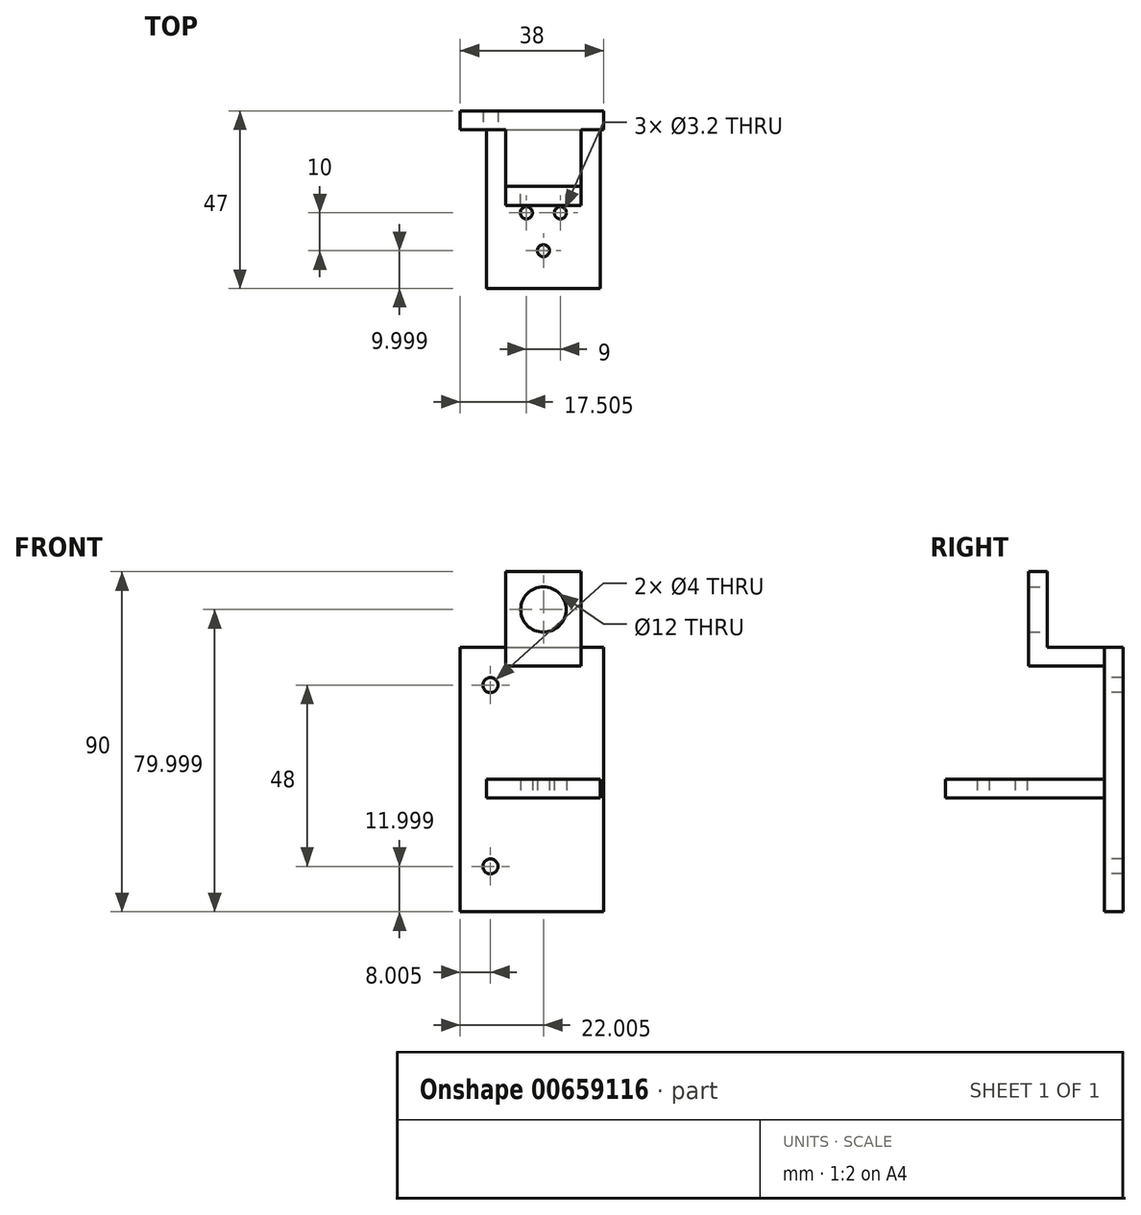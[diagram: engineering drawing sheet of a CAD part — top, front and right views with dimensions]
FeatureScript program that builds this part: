
annotation { "Feature Type Name" : "Feature", "Feature Type Description" : "" }
export const myFeature = defineFeature(function(context is Context, id is Id, definition is map)
    precondition{}
    {
        {
            var Q0;
            Q0=qCreatedBy(makeId("Top.planeOp"),FACE);
            var sketch = newSketch(context, id + "F0", { "sketchPlane" : qUnion([Q0])});
            skLineSegment(sketch, "E0.bottom", {"start": v(-60.29, 32.76) * mm, "end": v(-30.29, 32.76) * mm});
            skLineSegment(sketch, "E0.top", {"start": v(-60.29, 2.76) * mm, "end": v(-30.29, 2.76) * mm});
            skLineSegment(sketch, "E0.left", {"start": v(-60.29, 32.76) * mm, "end": v(-60.29, 2.76) * mm});
            skLineSegment(sketch, "E0.right", {"start": v(-30.29, 32.76) * mm, "end": v(-30.29, 2.76) * mm});
            skCircle(sketch, "E1", {"center": v(-49.79, 22.76) * mm, "radius": 1.6 * mm});
            skCircle(sketch, "E2", {"center": v(-40.79, 22.76) * mm, "radius": 1.6 * mm});
            skCircle(sketch, "E3", {"center": v(-45.29, 12.76) * mm, "radius": 1.6 * mm});
            skSolve(sketch);
        }
        {
            var Q0;
            Q0=makeQuery(id+"F0.imprint","IMPRINT",FACE,{"disambiguationData":[TD([[makeQuery(id+"F0.imprint","IMPRINT",EDGE,{"derivedFrom":sQuery(id+"F0.wireOp",EDGE,"E0.bottom")}),-1.0]])]});
            extrude(context, id + "F1", {"entities" : qUnion([Q0]), "depth" : 5 * mm, "offsetDistance" : 25 * mm});
        }
        {
            var Q0;
            Q0=makeQuery(id+"F1.opExtrude","SWEPT_FACE",FACE,{"disambiguationData":[OSD([sQuery(id+"F0.wireOp",EDGE,"E0.bottom")])]});
            extrude(context, id + "F2", {"entities" : qUnion([Q0]), "operationType" : NewBodyOperationType.ADD, "depth" : 12 * mm, "offsetDistance" : 25 * mm});
        }
        {
            var Q0;
            Q0=makeQuery(id+"F2.opExtrude","CAP_FACE",FACE,{"disambiguationData":[OSD([sQuery(id+"F0.wireOp",EDGE,"E0.bottom")])],"isStart":false});
            var sketch = newSketch(context, id + "F3", { "sketchPlane" : qUnion([Q0])});
            skLineSegment(sketch, "E4.bottom", {"start": v(67.29, -30.11) * mm, "end": v(29.29, -30.11) * mm});
            skLineSegment(sketch, "E4.top", {"start": v(67.29, 34.89) * mm, "end": v(29.29, 34.89) * mm});
            skLineSegment(sketch, "E4.left", {"start": v(67.29, -30.11) * mm, "end": v(67.29, 34.89) * mm});
            skLineSegment(sketch, "E4.right", {"start": v(29.29, -30.11) * mm, "end": v(29.29, 34.89) * mm});
            skCircle(sketch, "E5", {"center": v(59.29, 29.89) * mm, "radius": 2 * mm});
            skCircle(sketch, "E6", {"center": v(59.29, -18.11) * mm, "radius": 2 * mm});
            skSolve(sketch);
        }
        {
            var Q0;
            Q0=makeQuery(id+"F3.imprint","IMPRINT",FACE,{"disambiguationData":[TD([[makeQuery(id+"F3.imprint","IMPRINT",EDGE,{"derivedFrom":sQuery(id+"F3.wireOp",EDGE,"E4.bottom")}),-1.0]])]});
            var Q1;
            {var subQ0=sQuery(id+"F0.wireOp",EDGE,"E0.bottom");Q1=makeQuery(id+"F3.imprint","IMPRINT",FACE,{"disambiguationData":[TD([[makeQuery(id+"F3.imprint","IMPRINT",EDGE,{"derivedFrom":makeQuery(id+"F2.opExtrude","CAP_EDGE",EDGE,{"disambiguationData":[OSD([subQ0]),TDD([makeQuery(id+"F1.opExtrude","CAP_EDGE",EDGE,{"disambiguationData":[OSD([subQ0])],"isStart":true})])],"isStart":false})}),-1.0]])]});}
            extrude(context, id + "F4", {"entities" : qUnion([Q0, Q1]), "operationType" : NewBodyOperationType.ADD, "depth" : 5 * mm, "offsetDistance" : 25 * mm});
        }
        {
            var Q0;
            Q0=makeQuery(id+"F4.opExtrude","SWEPT_FACE",FACE,{"disambiguationData":[OSD([sQuery(id+"F3.wireOp",EDGE,"E4.top")])]});
            extrude(context, id + "F5", {"entities" : qUnion([Q0]), "operationType" : NewBodyOperationType.ADD, "depth" : 5 * mm, "offsetDistance" : 25 * mm});
        }
        {
            var Q0;
            {var subQ0=sQuery(id+"F3.wireOp",EDGE,"E4.top");Q0=makeQuery(id+"F5.boolean.opBoolean","MERGE",FACE,{"derivedFrom":[makeQuery(id+"F4.opExtrude","CAP_FACE",FACE,{"disambiguationData":[OSD([sQuery(id+"F3.wireOp",EDGE,"E4.bottom"),subQ0,sQuery(id+"F3.wireOp",EDGE,"E4.left"),sQuery(id+"F3.wireOp",EDGE,"E4.right"),sQuery(id+"F3.wireOp",EDGE,"E5"),sQuery(id+"F3.wireOp",EDGE,"E6")])],"isStart":true}),makeQuery(id+"F5.opExtrude","SWEPT_FACE",FACE,{"disambiguationData":[OSD([subQ0]),TDD([makeQuery(id+"F4.opExtrude","CAP_EDGE",EDGE,{"disambiguationData":[OSD([subQ0])],"isStart":true})])]})]});}
            var sketch = newSketch(context, id + "F6", { "sketchPlane" : qUnion([Q0])});
            skLineSegment(sketch, "E7.bottom", {"start": v(-55.29, 39.89) * mm, "end": v(-35.29, 39.89) * mm});
            skLineSegment(sketch, "E7.top", {"start": v(-55.29, 34.89) * mm, "end": v(-35.29, 34.89) * mm});
            skLineSegment(sketch, "E7.left", {"start": v(-55.29, 39.89) * mm, "end": v(-55.29, 34.89) * mm});
            skLineSegment(sketch, "E7.right", {"start": v(-35.29, 39.89) * mm, "end": v(-35.29, 34.89) * mm});
            skLineSegment(sketch, "E8", {"start": v(-45.29, 34.89) * mm, "end": v(-45.29, 5) * mm});
            skSolve(sketch);
        }
        {
            var Q0;
            Q0=makeQuery(id+"F6.imprint","IMPRINT",FACE,{"disambiguationData":[TD([[makeQuery(id+"F6.imprint","IMPRINT",EDGE,{"derivedFrom":sQuery(id+"F6.wireOp",EDGE,"E7.bottom")}),-1.0]])]});
            extrude(context, id + "F7", {"entities" : qUnion([Q0]), "operationType" : NewBodyOperationType.ADD, "depth" : 20 * mm, "offsetDistance" : 25 * mm});
        }
        {
            var Q0;
            Q0=makeQuery(id+"F7.boolean.opBoolean","MERGE",FACE,{"derivedFrom":[makeQuery(id+"F5.opExtrude","CAP_FACE",FACE,{"disambiguationData":[OSD([sQuery(id+"F3.wireOp",EDGE,"E4.top")])],"isStart":false}),makeQuery(id+"F7.opExtrude","SWEPT_FACE",FACE,{"disambiguationData":[OSD([sQuery(id+"F6.wireOp",EDGE,"E7.bottom")])]})]});
            var sketch = newSketch(context, id + "F8", { "sketchPlane" : qUnion([Q0])});
            skLineSegment(sketch, "E9.bottom", {"start": v(-55.29, 24.76) * mm, "end": v(-35.29, 24.76) * mm});
            skLineSegment(sketch, "E9.top", {"start": v(-55.29, 29.76) * mm, "end": v(-35.29, 29.76) * mm});
            skLineSegment(sketch, "E9.left", {"start": v(-55.29, 24.76) * mm, "end": v(-55.29, 29.76) * mm});
            skLineSegment(sketch, "E9.right", {"start": v(-35.29, 24.76) * mm, "end": v(-35.29, 29.76) * mm});
            skSolve(sketch);
        }
        {
            var Q0;
            Q0=makeQuery(id+"F8.imprint","IMPRINT",FACE,{"disambiguationData":[TD([[makeQuery(id+"F8.imprint","IMPRINT",EDGE,{"derivedFrom":sQuery(id+"F8.wireOp",EDGE,"E9.bottom")}),1.0]])]});
            extrude(context, id + "F9", {"entities" : qUnion([Q0]), "operationType" : NewBodyOperationType.ADD, "depth" : 20 * mm, "offsetDistance" : 25 * mm});
        }
        {
            var Q0;
            Q0=makeQuery(id+"F9.opExtrude","SWEPT_FACE",FACE,{"disambiguationData":[OSD([sQuery(id+"F8.wireOp",EDGE,"E9.top")])]});
            var sketch = newSketch(context, id + "F10", { "sketchPlane" : qUnion([Q0])});
            skCircle(sketch, "E10", {"center": v(45.29, 49.89) * mm, "radius": 6 * mm});
            skSolve(sketch);
        }
        {
            var Q0;
            Q0=makeQuery(id+"F10.imprint","IMPRINT",FACE,{"disambiguationData":[TD([[makeQuery(id+"F10.imprint","IMPRINT",EDGE,{"derivedFrom":sQuery(id+"F10.wireOp",EDGE,"E10")}),1.0]])]});
            extrude(context, id + "F11", {"entities" : qUnion([Q0]), "operationType" : NewBodyOperationType.REMOVE, "oppositeDirection" : true, "depth" : 5 * mm, "offsetDistance" : 25 * mm});
        }
    });
